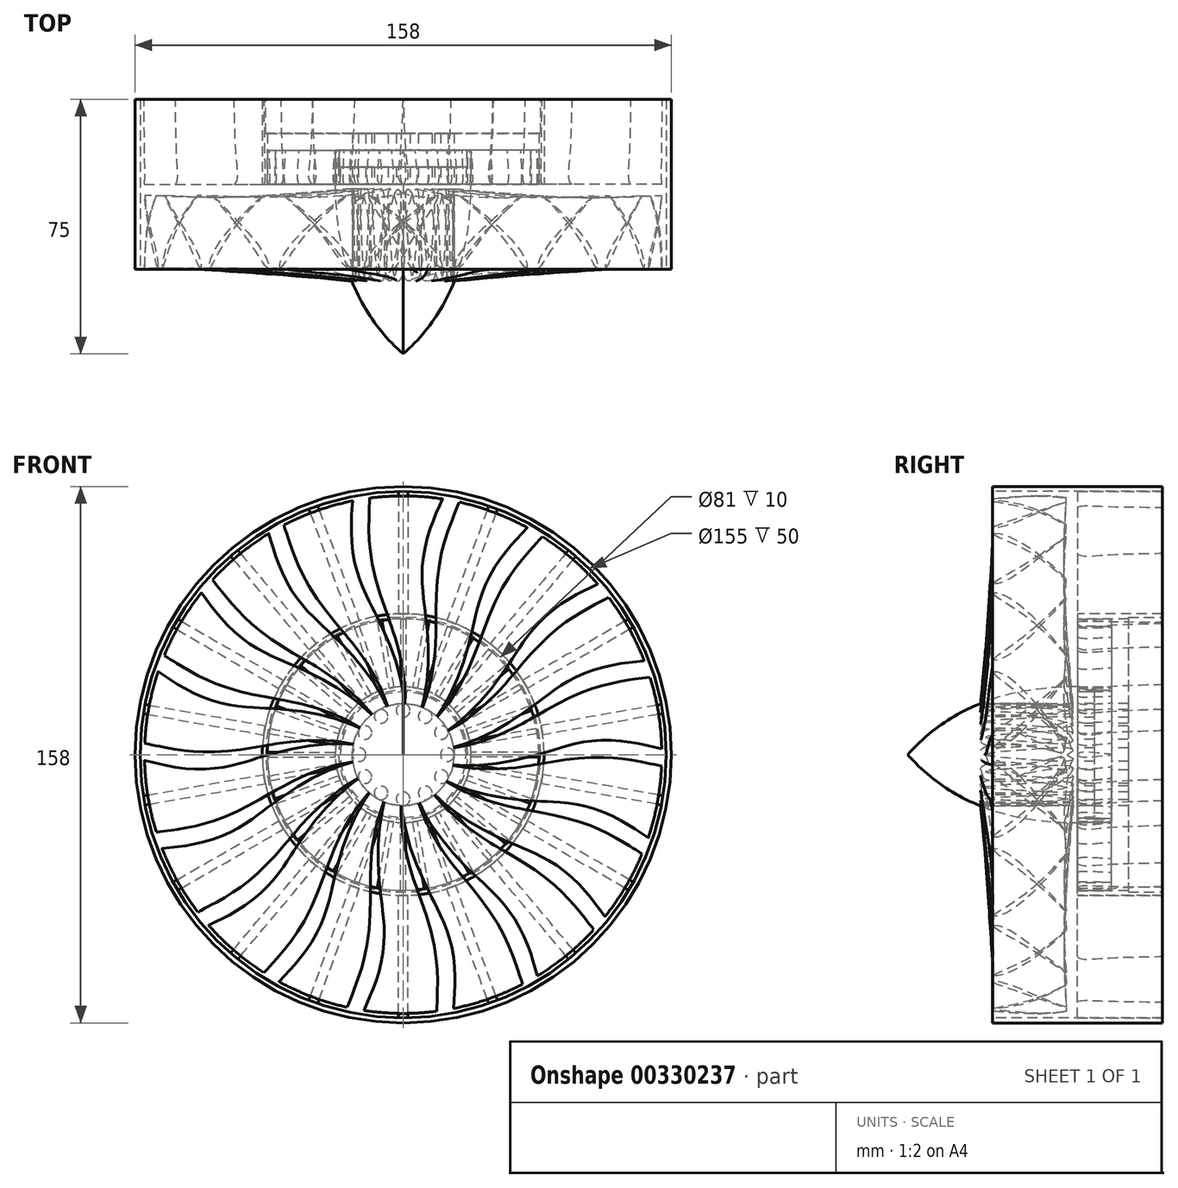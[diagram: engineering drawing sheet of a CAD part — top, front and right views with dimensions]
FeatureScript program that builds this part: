
annotation { "Feature Type Name" : "Feature", "Feature Type Description" : "" }
export const myFeature = defineFeature(function(context is Context, id is Id, definition is map)
    precondition{}
    {
        {
            var Q0;
            Q0=qCreatedBy(makeId("Front.planeOp"),FACE);
            var sketch = newSketch(context, id + "F0", { "sketchPlane" : qUnion([Q0]), "disableImprinting" : false});
            skLineSegment(sketch, "E0", {"start": v(0, 0) * mm, "end": v(3.8, 0) * mm});
            skLineSegment(sketch, "E1", {"start": v(0, 0) * mm, "end": v(-3.81, 0) * mm});
            skLineSegment(sketch, "E2", {"start": v(-19.05, 76.2) * mm, "end": v(0, 76.2) * mm});
            skLineSegment(sketch, "E3", {"start": v(0, 76.2) * mm, "end": v(19.05, 76.2) * mm});
            skPoint(sketch, "E4.2.internal.snap0", {"position": v(-9.53, 76.2) * mm});
            skFitSpline(sketch, "E5", {"points": [v(-19.05, 76.2) * mm, v(-3.81, 0) * mm], "startDerivative": vector(0, -114.3) * mm, "endDerivative": vector(-11.43, -114.3) * mm});
            skFitSpline(sketch, "E6", {"points": [v(19.05, 76.2) * mm, v(3.81, 0) * mm], "startDerivative": vector(-57.15, -114.3) * mm, "endDerivative": vector(-45.72, -57.15) * mm});
            skSolve(sketch);
        }
        {
            var Q0;
            Q0=qCreatedBy(makeId("Top.planeOp"),FACE);
            var sketch = newSketch(context, id + "F1", { "sketchPlane" : qUnion([Q0])});
            skFitSpline(sketch, "E7.MirrorC", {"points": [v(-1.36, -15.24) * mm, v(0.64, -10) * mm, v(-1.36, 15.24) * mm, v(-0.56, 0) * mm, v(-1.36, -15.24) * mm]});
            skSolve(sketch);
        }
        {
            var Q0;
            Q0=qCreatedBy(makeId("Top.planeOp"),FACE);
            cPlane(context, id + "F2", {"entities" : qUnion([Q0]), "cplaneType" : CPlaneType.OFFSET, "offset" : 76.2 * mm, "width" : 150 * mm, "height" : 150 * mm});
        }
        {
            var Q0;
            Q0=qCreatedBy(id+"F2.planeOp",FACE);
            var sketch = newSketch(context, id + "F3", { "sketchPlane" : qUnion([Q0])});
            skFitSpline(sketch, "E8.MirrorC", {"points": [v(11.74, -9.81) * mm, v(9.45, -4.7) * mm, v(-9.81, 11.74) * mm, v(1.53, 1.53) * mm, v(11.74, -9.81) * mm]});
            skSolve(sketch);
        }
        {
            var Q0;
            Q0=sQuery(id+"F0.wireOp",EDGE,"E5");
            var Q1;
            Q1=makeQuery(id+"F3.imprint","IMPRINT",FACE,{"disambiguationData":[TD([[makeQuery(id+"F3.imprint","IMPRINT",EDGE,{"derivedFrom":sQuery(id+"F3.wireOp",EDGE,"E8.MirrorC")}),1.0]])]});
            var Q2;
            Q2=makeQuery(id+"F1.imprint","IMPRINT",FACE,{"disambiguationData":[TD([[makeQuery(id+"F1.imprint","IMPRINT",EDGE,{"derivedFrom":sQuery(id+"F1.wireOp",EDGE,"E7.MirrorC")}),1.0]])]});
            loft(context, id + "F4", {"addSections" : true, "spine" : qUnion([Q0]), "sectionCount" : 4, "sheetProfilesArray" : [{ "sheetProfileEntities" : qUnion([Q1]) }, { "sheetProfileEntities" : qUnion([Q2]) }], "trimGuidesByProfiles" : true});
        }
        {
            var Q0;
            Q0=qCreatedBy(makeId("Front.planeOp"),FACE);
            var sketch = newSketch(context, id + "F5", { "sketchPlane" : qUnion([Q0])});
            skCircle(sketch, "E9", {"center": v(0, 0) * mm, "radius": 76.2 * mm});
            skSolve(sketch);
        }
        {
            var Q0;
            Q0 = qSketchRegion(id + "F5", true);
            extrude(context, id + "F6", {"entities" : qUnion([Q0]), "operationType" : NewBodyOperationType.INTERSECT, "depth" : 30 * mm, "offsetDistance" : 25 * mm, "symmetric" : true});
        }
        {
            var Q0;
            Q0=qCreatedBy(makeId("Front.planeOp"),FACE);
            var sketch = newSketch(context, id + "F7", { "sketchPlane" : qUnion([Q0])});
            skCircle(sketch, "E10", {"center": v(0, 0) * mm, "radius": 15 * mm});
            skSolve(sketch);
        }
        {
            var Q0;
            Q0 = qSketchRegion(id + "F7", true);
            extrude(context, id + "F8", {"entities" : qUnion([Q0]), "operationType" : NewBodyOperationType.REMOVE, "oppositeDirection" : true, "depth" : 30 * mm, "offsetDistance" : 25 * mm, "symmetric" : true});
        }
        {
            var Q0;
            Q0=makeQuery(id+"F4.opLoft","SWEPT_BODY",BODY,{"disambiguationData":[OSD([makeQuery(id+"F1.imprint","IMPRINT",FACE,{"disambiguationData":[TD([[makeQuery(id+"F1.imprint","IMPRINT",EDGE,{"derivedFrom":sQuery(id+"F1.wireOp",EDGE,"E7.MirrorC")}),1.0]])]}),makeQuery(id+"F3.imprint","IMPRINT",FACE,{"disambiguationData":[TD([[makeQuery(id+"F3.imprint","IMPRINT",EDGE,{"derivedFrom":sQuery(id+"F3.wireOp",EDGE,"E8.MirrorC")}),1.0]])]})])]});
            var Q1;
            Q1=sQuery(id+"F5.wireOp",EDGE,"E9");
            circularPattern(context, id + "F9", {"entities" : qUnion([Q0]), "axis" : qUnion([Q1]), "angle" : 360 * degree, "instanceCount" : 18, "equalSpace" : true, "fullFeaturePattern" : false});
        }
        {
            var Q0;
            Q0=qCreatedBy(makeId("Right.planeOp"),FACE);
            var sketch = newSketch(context, id + "F10", { "sketchPlane" : qUnion([Q0])});
            skLineSegment(sketch, "E11", {"start": v(0, 0) * mm, "end": v(15, 0) * mm});
            skLineSegment(sketch, "E12", {"start": v(0, 0) * mm, "end": v(-35, 0) * mm});
            skLineSegment(sketch, "E13", {"start": v(15, 0) * mm, "end": v(15, 20) * mm});
            skFitSpline(sketch, "E14", {"points": [v(15, 20) * mm, v(-35, 0) * mm], "startDerivative": vector(-45, 0) * mm, "endDerivative": vector(-45, -51) * mm});
            skLineSegment(sketch, "E15", {"start": v(15, 20) * mm, "end": v(56.2, 20) * mm});
            skLineSegment(sketch, "E16", {"start": v(56.2, 20) * mm, "end": v(56.2, 0) * mm});
            skLineSegment(sketch, "E17", {"start": v(56.2, 0) * mm, "end": v(15, 0) * mm});
            skSolve(sketch);
        }
        {
            var Q0;
            Q0=makeQuery(id+"F10.imprint","IMPRINT",FACE,{"disambiguationData":[TD([[makeQuery(id+"F10.imprint","IMPRINT",EDGE,{"derivedFrom":sQuery(id+"F10.wireOp",EDGE,"E11")}),1.0]])]});
            var Q1;
            Q1=sQuery(id+"F10.wireOp",EDGE,"E12");
            revolve(context, id + "F11", {"surfaceOperationType" : NewSurfaceOperationType.NEW, "entities" : qUnion([Q0]), "axis" : qUnion([Q1]), "revolveType" : RevolveType.FULL});
        }
        {
            var Q0;
            Q0=makeQuery(id+"F11.opRevolve","SWEPT_FACE",FACE,{"disambiguationData":[OSD([sQuery(id+"F10.wireOp",EDGE,"E13")])]});
            var sketch = newSketch(context, id + "F12", { "sketchPlane" : qUnion([Q0])});
            skCircle(sketch, "E18", {"center": v(0, 0) * mm, "radius": 18.5 * mm});
            skCircle(sketch, "E19", {"center": v(0, 0) * mm, "radius": 20 * mm});
            skCircle(sketch, "E20", {"center": v(0, 0) * mm, "radius": 40 * mm});
            skCircle(sketch, "E21", {"center": v(0, 0) * mm, "radius": 41.5 * mm});
            skCircle(sketch, "E22", {"center": v(0, 0) * mm, "radius": 77.5 * mm});
            skCircle(sketch, "E23", {"center": v(0, 0) * mm, "radius": 79 * mm});
            skSolve(sketch);
        }
        {
            var Q0;
            Q0=makeQuery(id+"F12.imprint","IMPRINT",FACE,{"disambiguationData":[TD([[makeQuery(id+"F12.imprint","IMPRINT",EDGE,{"derivedFrom":sQuery(id+"F12.wireOp",EDGE,"E18")}),-1.0]])]});
            extrude(context, id + "F13", {"entities" : qUnion([Q0]), "depth" : 10 * mm, "offsetDistance" : 25 * mm});
        }
        {
            var Q0;
            Q0=qCreatedBy(makeId("Top.planeOp"),FACE);
            cPlane(context, id + "F14", {"entities" : qUnion([Q0]), "cplaneType" : CPlaneType.OFFSET, "offset" : 20 * mm, "width" : 150 * mm, "height" : 150 * mm});
        }
        {
            var Q0;
            Q0=qCreatedBy(id+"F14.planeOp",FACE);
            var sketch = newSketch(context, id + "F15", { "sketchPlane" : qUnion([Q0])});
            skFitSpline(sketch, "E24", {"points": [v(0, 15) * mm, v(0.6, 16) * mm, v(0.4, 21.67) * mm, v(0, 25) * mm, v(-0.4, 21.67) * mm, v(-0.6, 16) * mm, v(0, 15) * mm]});
            skSolve(sketch);
        }
        {
            var Q0;
            Q0 = qSketchRegion(id + "F15", true);
            extrude(context, id + "F16", {"entities" : qUnion([Q0]), "depth" : 20 * mm, "offsetDistance" : 25 * mm});
        }
        {
            var Q0;
            Q0=makeQuery(id+"F16.opExtrude","SWEPT_BODY",BODY,{"disambiguationData":[OSD([sQuery(id+"F15.wireOp",EDGE,"E24")])]});
            var Q1;
            Q1=makeQuery(id+"F13.opExtrude","CAP_EDGE",EDGE,{"disambiguationData":[OSD([sQuery(id+"F12.wireOp",EDGE,"E19")])],"isStart":false});
            circularPattern(context, id + "F17", {"entities" : qUnion([Q0]), "axis" : qUnion([Q1]), "angle" : 360 * degree, "instanceCount" : 36, "equalSpace" : true, "fullFeaturePattern" : false});
        }
        {
            var Q0;
            Q0=makeQuery(id+"F12.imprint","IMPRINT",FACE,{"disambiguationData":[TD([[makeQuery(id+"F12.imprint","IMPRINT",EDGE,{"derivedFrom":sQuery(id+"F12.wireOp",EDGE,"E20")}),-1.0]])]});
            extrude(context, id + "F18", {"entities" : qUnion([Q0]), "depth" : 25 * mm, "offsetDistance" : 25 * mm});
        }
        {
            var Q0;
            Q0=makeQuery(id+"F12.imprint","IMPRINT",FACE,{"disambiguationData":[TD([[makeQuery(id+"F12.imprint","IMPRINT",EDGE,{"derivedFrom":sQuery(id+"F12.wireOp",EDGE,"E22")}),-1.0]])]});
            extrude(context, id + "F19", {"entities" : qUnion([Q0]), "depth" : 50 * mm, "offsetDistance" : 25 * mm, "symmetric" : true});
        }
        {
            var Q0;
            Q0=qCreatedBy(makeId("Top.planeOp"),FACE);
            cPlane(context, id + "F20", {"entities" : qUnion([Q0]), "cplaneType" : CPlaneType.OFFSET, "offset" : 41.5 * mm, "width" : 150 * mm, "height" : 150 * mm});
        }
        {
            var Q0;
            Q0=qCreatedBy(id+"F20.planeOp",FACE);
            var sketch = newSketch(context, id + "F21", { "sketchPlane" : qUnion([Q0])});
            skFitSpline(sketch, "E25", {"points": [v(0, 15) * mm, v(1.2, 16.33) * mm, v(0.75, 24.08) * mm, v(0, 40) * mm, v(-0.75, 24.08) * mm, v(-1.2, 16.33) * mm, v(0, 15) * mm]});
            skSolve(sketch);
        }
        {
            var Q0;
            Q0 = qSketchRegion(id + "F21", true);
            extrude(context, id + "F22", {"entities" : qUnion([Q0]), "depth" : 36 * mm, "offsetDistance" : 25 * mm});
        }
        {
            var Q0;
            Q0=makeQuery(id+"F22.opExtrude","SWEPT_BODY",BODY,{"disambiguationData":[OSD([sQuery(id+"F21.wireOp",EDGE,"E25")])]});
            var Q1;
            Q1=makeQuery(id+"F18.opExtrude","SWEPT_FACE",FACE,{"disambiguationData":[OSD([sQuery(id+"F12.wireOp",EDGE,"E21")])]});
            circularPattern(context, id + "F23", {"entities" : qUnion([Q0]), "axis" : qUnion([Q1]), "angle" : 360 * degree, "instanceCount" : 18, "equalSpace" : true, "fullFeaturePattern" : false});
        }
        {
            var Q0;
            Q0=makeQuery(id+"F12.imprint","IMPRINT",FACE,{"disambiguationData":[TD([[makeQuery(id+"F12.imprint","IMPRINT",EDGE,{"derivedFrom":sQuery(id+"F12.wireOp",EDGE,"E18")}),1.0]])]});
            var sketch = newSketch(context, id + "F24", { "sketchPlane" : qUnion([Q0])});
            skCircle(sketch, "E26", {"center": v(0, 13) * mm, "radius": 2 * mm});
            skCircle(sketch, "E27.1.0", {"center": v(-6.5, 11.26) * mm, "radius": 2 * mm});
            skCircle(sketch, "E27.2.0", {"center": v(-11.26, 6.5) * mm, "radius": 2 * mm});
            skCircle(sketch, "E27.3.0", {"center": v(-13, 0) * mm, "radius": 2 * mm});
            skCircle(sketch, "E27.4.0", {"center": v(-11.26, -6.5) * mm, "radius": 2 * mm});
            skCircle(sketch, "E27.5.0", {"center": v(-6.5, -11.26) * mm, "radius": 2 * mm});
            skCircle(sketch, "E27.6.0", {"center": v(0, -13) * mm, "radius": 2 * mm});
            skCircle(sketch, "E27.7.0", {"center": v(6.5, -11.26) * mm, "radius": 2 * mm});
            skCircle(sketch, "E27.8.0", {"center": v(11.26, -6.5) * mm, "radius": 2 * mm});
            skCircle(sketch, "E27.9.0", {"center": v(13, 0) * mm, "radius": 2 * mm});
            skCircle(sketch, "E27.10.0", {"center": v(11.26, 6.5) * mm, "radius": 2 * mm});
            skCircle(sketch, "E27.11.0", {"center": v(6.5, 11.26) * mm, "radius": 2 * mm});
            skPoint(sketch, "E27.center", {"position": v(0, 0) * mm});
            skSolve(sketch);
        }
        {
            var Q0;
            Q0 = qSketchRegion(id + "F24", true);
            extrude(context, id + "F25", {"entities" : qUnion([Q0]), "operationType" : NewBodyOperationType.ADD, "depth" : 25 * mm, "offsetDistance" : 25 * mm});
        }
        {
            var Q0;
            Q0=makeQuery(id+"F13.opExtrude","CAP_FACE",FACE,{"disambiguationData":[OSD([sQuery(id+"F12.wireOp",EDGE,"E18"),sQuery(id+"F12.wireOp",EDGE,"E19")])],"isStart":false});
            var sketch = newSketch(context, id + "F26", { "sketchPlane" : qUnion([Q0])});
            skCircle(sketch, "E28", {"center": v(0, 0) * mm, "radius": 19 * mm});
            skSolve(sketch);
        }
        {
            var Q0;
            Q0 = qSketchRegion(id + "F26", true);
            extrude(context, id + "F27", {"entities" : qUnion([Q0]), "operationType" : NewBodyOperationType.REMOVE, "oppositeDirection" : true, "depth" : 5 * mm, "offsetDistance" : 25 * mm});
        }
        {
            var Q0;
            Q0=makeQuery(id+"F18.opExtrude","CAP_FACE",FACE,{"disambiguationData":[OSD([sQuery(id+"F12.wireOp",EDGE,"E20"),sQuery(id+"F12.wireOp",EDGE,"E21")])],"isStart":false});
            var sketch = newSketch(context, id + "F28", { "sketchPlane" : qUnion([Q0])});
            skCircle(sketch, "E29", {"center": v(0, 0) * mm, "radius": 40.5 * mm});
            skSolve(sketch);
        }
        {
            var Q0;
            Q0 = qSketchRegion(id + "F28", true);
            extrude(context, id + "F29", {"entities" : qUnion([Q0]), "operationType" : NewBodyOperationType.REMOVE, "oppositeDirection" : true, "depth" : 10 * mm, "offsetDistance" : 25 * mm});
        }
    });
